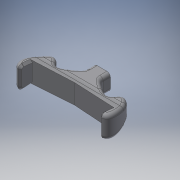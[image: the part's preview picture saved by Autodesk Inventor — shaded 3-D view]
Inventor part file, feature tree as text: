
AUTODESK INVENTOR PART (.ipt)
format: ipt  version: 2017 (Build 210142000, 142)  size: 544,768 bytes
history: native  units: in
note: dims shown in document units (in); Inventor stores cm internally (conversion verified against a paired STEP export)
features: extrude x4, sketch x3, fillet x1, chamfer x1, projected_geometry x1
ambient origin geometry x8: Origin, YZ Plane, XZ Plane, XY Plane, X Axis, Y Axis, Z Axis, Center Point
bodies: Solid1 (feature_tree)
feature tree (10):
  extrude  "Extrusion1"  Depth=2.25in
  extrude  "Extrusion2"  Depth=0.3287in
  sketch  "Sketch3"  dims[d5=0.4724in d6=0.0in d7=0.4724in d9=15.748in d10=0.0in d11=15.748in d12=15.748in d13=0.0in d14=0.5in d15=0.5in d16=0.4724in d17=15.748in d19=0.1in d20=0.0591in d21=0.125in d22=45.0deg]
  extrude  "Extrusion3"  Depth=0.4724in
  extrude  "Extrusion4"  Depth=15.748in TaperAngle=0.0deg
  fillet  "Fillet2"  Radius=15.748in
  chamfer  "Chamfer1"  Distance=15.748in
  sketch  "Sketch1"  dims[d0=0.6299in d1=0.0in d2=2.25in]
  sketch  "Sketch2"  dims[d3=0.3543in d4=0.3287in]
  projected_geometry  "Projected Loop1"
